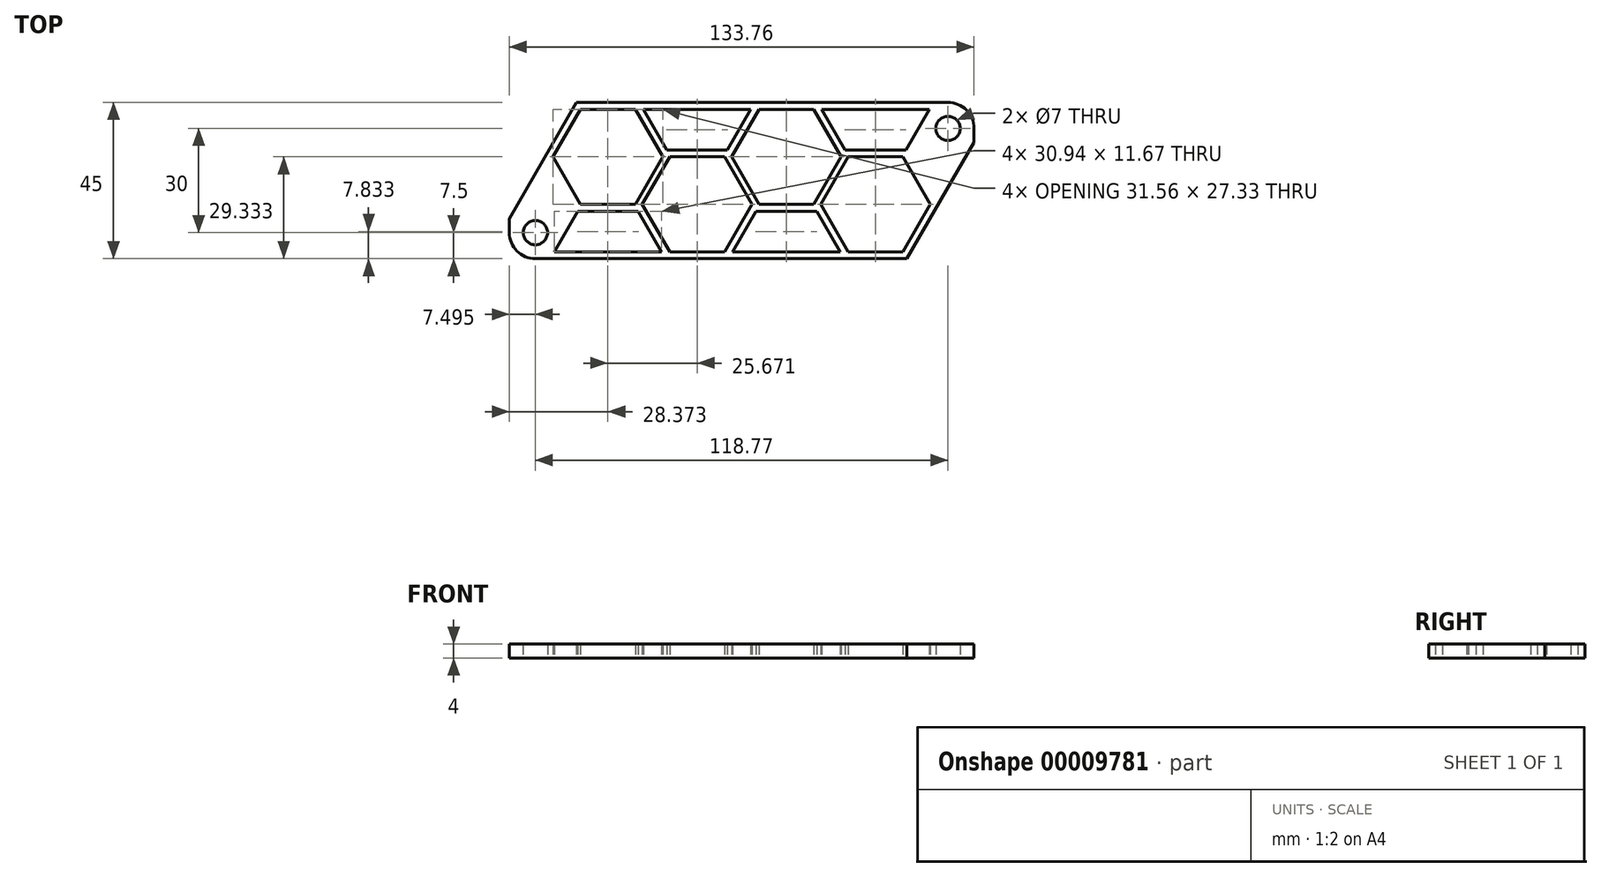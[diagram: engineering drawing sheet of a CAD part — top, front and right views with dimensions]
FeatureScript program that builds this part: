
annotation { "Feature Type Name" : "Feature", "Feature Type Description" : "" }
export const myFeature = defineFeature(function(context is Context, id is Id, definition is map)
    precondition{}
    {
        {
            var Q0;
            Q0=qCreatedBy(makeId("Top.planeOp"),FACE);
            var sketch = newSketch(context, id + "F0", { "sketchPlane" : qUnion([Q0])});
            skLineSegment(sketch, "E0.rect.top", {"start": v(59.38, 22.5) * mm, "end": v(-47.55, 22.5) * mm});
            skLineSegment(sketch, "E0.rect.right", {"start": v(-66.88, -15) * mm, "end": v(-66.88, -10.99) * mm});
            skPoint(sketch, "E0.rect.middle", {"position": v(0, 0) * mm});
            skCircle(sketch, "E1", {"center": v(-59.38, -15) * mm, "radius": 3.5 * mm});
            skCircle(sketch, "E2", {"center": v(59.38, 15) * mm, "radius": 3.5 * mm});
            skCircle(sketch, "E3.cCircle", {"center": v(-38.5, 6.83) * mm, "radius": 13.67 * mm, "construction": true});
            skLineSegment(sketch, "E3.0", {"start": v(-22.73, 6.83) * mm, "end": v(-30.62, -6.83) * mm});
            skLineSegment(sketch, "E3.1", {"start": v(-30.62, -6.83) * mm, "end": v(-46.4, -6.83) * mm});
            skLineSegment(sketch, "E3.2", {"start": v(-46.4, -6.83) * mm, "end": v(-54.29, 6.83) * mm});
            skLineSegment(sketch, "E3.3", {"start": v(-54.29, 6.83) * mm, "end": v(-46.4, 20.5) * mm});
            skLineSegment(sketch, "E3.4", {"start": v(-46.4, 20.5) * mm, "end": v(-30.62, 20.5) * mm});
            skLineSegment(sketch, "E3.5", {"start": v(-30.62, 20.5) * mm, "end": v(-22.73, 6.83) * mm});
            skCircle(sketch, "E4.cCircle", {"center": v(-12.84, -6.83) * mm, "radius": 13.67 * mm, "construction": true});
            skLineSegment(sketch, "E4.0", {"start": v(2.95, -6.83) * mm, "end": v(-4.95, -20.5) * mm});
            skLineSegment(sketch, "E4.1", {"start": v(-4.95, -20.5) * mm, "end": v(-20.73, -20.5) * mm});
            skLineSegment(sketch, "E4.2", {"start": v(-20.73, -20.5) * mm, "end": v(-28.62, -6.83) * mm});
            skLineSegment(sketch, "E4.3", {"start": v(-28.62, -6.83) * mm, "end": v(-20.73, 6.83) * mm});
            skLineSegment(sketch, "E4.4", {"start": v(-20.73, 6.83) * mm, "end": v(-4.95, 6.83) * mm});
            skLineSegment(sketch, "E4.5", {"start": v(-4.95, 6.83) * mm, "end": v(2.95, -6.83) * mm});
            skCircle(sketch, "E5.cCircle", {"center": v(12.84, 6.83) * mm, "radius": 13.67 * mm, "construction": true});
            skLineSegment(sketch, "E5.0", {"start": v(28.62, 6.83) * mm, "end": v(20.73, -6.83) * mm});
            skLineSegment(sketch, "E5.1", {"start": v(20.73, -6.83) * mm, "end": v(4.95, -6.83) * mm});
            skLineSegment(sketch, "E5.2", {"start": v(4.95, -6.83) * mm, "end": v(-2.95, 6.83) * mm});
            skLineSegment(sketch, "E5.3", {"start": v(-2.95, 6.83) * mm, "end": v(4.95, 20.5) * mm});
            skLineSegment(sketch, "E5.4", {"start": v(4.95, 20.5) * mm, "end": v(20.73, 20.5) * mm});
            skLineSegment(sketch, "E5.5", {"start": v(20.73, 20.5) * mm, "end": v(28.62, 6.83) * mm});
            skPoint(sketch, "E5.0.midPoint", {"position": v(24.67, 0) * mm});
            skCircle(sketch, "E6.cCircle", {"center": v(38.5, -6.83) * mm, "radius": 13.67 * mm, "construction": true});
            skLineSegment(sketch, "E6.0", {"start": v(54.29, -6.83) * mm, "end": v(46.4, -20.5) * mm});
            skLineSegment(sketch, "E6.1", {"start": v(46.4, -20.5) * mm, "end": v(30.62, -20.5) * mm});
            skLineSegment(sketch, "E6.2", {"start": v(30.62, -20.5) * mm, "end": v(22.73, -6.83) * mm});
            skLineSegment(sketch, "E6.3", {"start": v(22.73, -6.83) * mm, "end": v(30.62, 6.83) * mm});
            skLineSegment(sketch, "E6.4", {"start": v(30.62, 6.83) * mm, "end": v(46.4, 6.83) * mm});
            skLineSegment(sketch, "E6.5", {"start": v(46.4, 6.83) * mm, "end": v(54.29, -6.83) * mm});
            skLineSegment(sketch, "E7", {"start": v(-2.64, -20.5) * mm, "end": v(4.1, -8.83) * mm});
            skLineSegment(sketch, "E8", {"start": v(4.1, -8.83) * mm, "end": v(21.57, -8.83) * mm});
            skLineSegment(sketch, "E9", {"start": v(21.57, -8.83) * mm, "end": v(28.3, -20.5) * mm});
            skLineSegment(sketch, "E10", {"start": v(28.3, -20.5) * mm, "end": v(-2.64, -20.5) * mm});
            skLineSegment(sketch, "E11", {"start": v(-28.3, 20.5) * mm, "end": v(-21.57, 8.83) * mm});
            skLineSegment(sketch, "E12", {"start": v(-21.57, 8.83) * mm, "end": v(-4.1, 8.83) * mm});
            skLineSegment(sketch, "E13", {"start": v(-4.1, 8.83) * mm, "end": v(2.64, 20.5) * mm});
            skLineSegment(sketch, "E14", {"start": v(2.64, 20.5) * mm, "end": v(-28.3, 20.5) * mm});
            skLineSegment(sketch, "E15", {"start": v(23.04, 20.5) * mm, "end": v(29.77, 8.83) * mm});
            skLineSegment(sketch, "E16", {"start": v(29.77, 8.83) * mm, "end": v(47.24, 8.83) * mm});
            skLineSegment(sketch, "E17", {"start": v(47.24, 8.83) * mm, "end": v(53.98, 20.5) * mm});
            skLineSegment(sketch, "E18", {"start": v(53.98, 20.5) * mm, "end": v(23.04, 20.5) * mm});
            skLineSegment(sketch, "E19", {"start": v(-53.98, -20.5) * mm, "end": v(-47.24, -8.83) * mm});
            skLineSegment(sketch, "E20", {"start": v(-47.24, -8.83) * mm, "end": v(-29.77, -8.83) * mm});
            skLineSegment(sketch, "E21", {"start": v(-29.77, -8.83) * mm, "end": v(-23.04, -20.5) * mm});
            skLineSegment(sketch, "E22", {"start": v(-23.04, -20.5) * mm, "end": v(-53.98, -20.5) * mm});
            skLineSegment(sketch, "E23", {"start": v(-47.55, 22.5) * mm, "end": v(-66.88, -10.99) * mm});
            skLineSegment(sketch, "E24", {"start": v(47.55, -22.5) * mm, "end": v(-59.38, -22.5) * mm});
            skLineSegment(sketch, "E25", {"start": v(66.88, 10.99) * mm, "end": v(66.88, 15) * mm});
            skLineSegment(sketch, "E26", {"start": v(47.55, -22.5) * mm, "end": v(66.88, 10.99) * mm});
            skArc(sketch, "E27", {"start": v(-66.88, -15) * mm, "mid": v(-64.69, -20.3) * mm, "end": v(-59.38, -22.5) * mm});
            skArc(sketch, "E28", {"start": v(66.88, 15) * mm, "mid": v(64.69, 20.3) * mm, "end": v(59.38, 22.5) * mm});
            skSolve(sketch);
        }
        {
            var Q0;
            Q0=makeQuery(id+"F0.imprint","IMPRINT",FACE,{"disambiguationData":[TD([[makeQuery(id+"F0.imprint","IMPRINT",EDGE,{"derivedFrom":sQuery(id+"F0.wireOp",EDGE,"E0.rect.top")}),1.0]])]});
            extrude(context, id + "F1", {"entities" : qUnion([Q0]), "depth" : 4 * mm});
        }
    });
